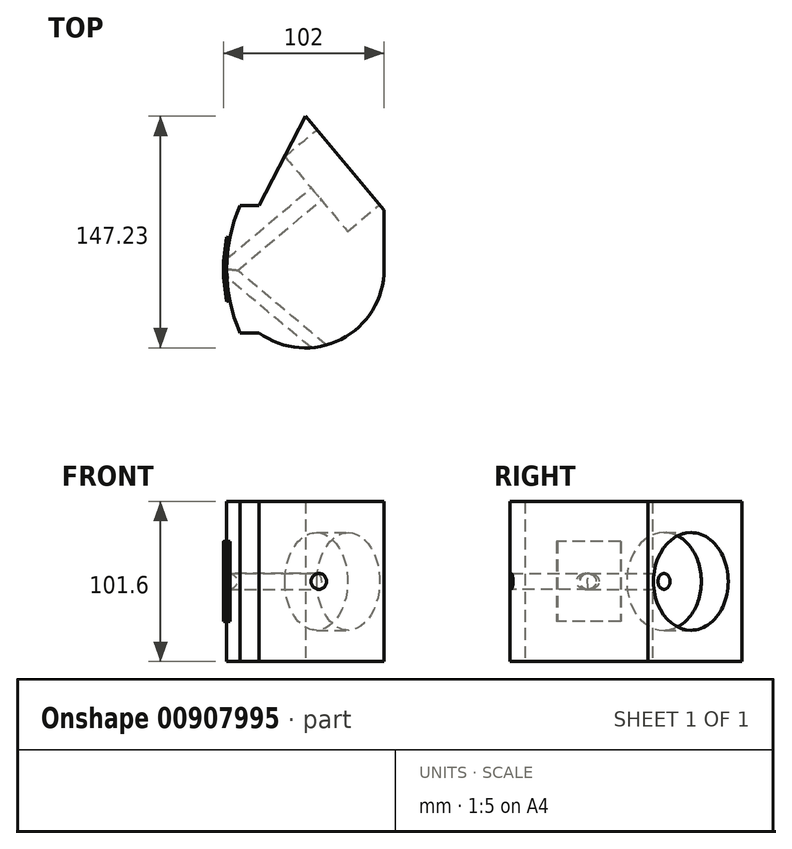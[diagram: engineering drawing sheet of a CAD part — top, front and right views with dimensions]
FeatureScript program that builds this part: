
annotation { "Feature Type Name" : "Feature", "Feature Type Description" : "" }
export const myFeature = defineFeature(function(context is Context, id is Id, definition is map)
    precondition{}
    {
        {
            var Q0;
            Q0=qCreatedBy(makeId("Top.planeOp"),FACE);
            var sketch = newSketch(context, id + "F0", { "sketchPlane" : qUnion([Q0])});
            skCircle(sketch, "E0", {"center": v(0, 0) * mm, "radius": 50 * mm});
            skLineSegment(sketch, "E1", {"start": v(-50, 0) * mm, "end": v(8.68, 49.24) * mm});
            skLineSegment(sketch, "E2", {"start": v(8.68, 49.24) * mm, "end": v(8.68, -49.24) * mm, "construction": true});
            skLineSegment(sketch, "E3", {"start": v(47.6, -81.9) * mm, "end": v(-50, 0) * mm});
            skPoint(sketch, "E4", {"position": v(8.68, 0) * mm});
            skLineSegment(sketch, "E5", {"start": v(-50, 0) * mm, "end": v(-50, 56.97) * mm, "construction": true});
            skLineSegment(sketch, "E6.MirrorCS", {"start": v(-50, 0) * mm, "end": v(-108.68, 49.24) * mm});
            skLineSegment(sketch, "E7", {"start": v(-50, 0) * mm, "end": v(8.68, 0) * mm, "construction": true});
            skLineSegment(sketch, "E8", {"start": v(0, 0) * mm, "end": v(8.68, 49.24) * mm, "construction": true});
            skSolve(sketch);
        }
        {
            var Q0;
            Q0=qCreatedBy(makeId("Top.planeOp"),FACE);
            var sketch = newSketch(context, id + "F1", { "sketchPlane" : qUnion([Q0])});
            skArc(sketch, "E9", {"start": v(-47.98, 20) * mm, "mid": v(-50, 0) * mm, "end": v(-47.98, -20) * mm});
            skArc(sketch, "E10", {"start": v(-49.94, 20.4) * mm, "mid": v(-52, 0) * mm, "end": v(-49.94, -20.4) * mm});
            skLineSegment(sketch, "E11", {"start": v(-49.94, 20.4) * mm, "end": v(-47.98, 20) * mm});
            skLineSegment(sketch, "E12", {"start": v(-47.98, -20) * mm, "end": v(-49.94, -20.4) * mm});
            skSolve(sketch);
        }
        {
            var Q0;
            Q0=qSketchRegion(id+"F1",true);
            extrude(context, id + "F2", {"entities" : qUnion([Q0]), "depth" : 25.4 * mm, "offsetDistance" : 25.4 * mm, "hasSecondDirection" : true, "secondDirectionOppositeDirection" : true, "secondDirectionDepth" : 25.4 * mm});
        }
        {
            var Q0;
            Q0=qCreatedBy(makeId("Top.planeOp"),FACE);
            var sketch = newSketch(context, id + "F3", { "sketchPlane" : qUnion([Q0])});
            skArc(sketch, "E13", {"start": v(-41.48, 40.4) * mm, "mid": v(-50, 0) * mm, "end": v(-41.48, -40.4) * mm});
            skLineSegment(sketch, "E14", {"start": v(-41.48, 40.4) * mm, "end": v(-29.46, 40.4) * mm});
            skLineSegment(sketch, "E15", {"start": v(-41.48, -40.4) * mm, "end": v(-29.46, -40.4) * mm});
            skArc(sketch, "E16", {"start": v(-29.46, -40.4) * mm, "mid": v(22.66, -44.57) * mm, "end": v(50, 0) * mm});
            skLineSegment(sketch, "E17", {"start": v(0, 97.23) * mm, "end": v(50, 37.64) * mm});
            skLineSegment(sketch, "E18", {"start": v(50, 37.64) * mm, "end": v(50, 0) * mm});
            skLineSegment(sketch, "E19", {"start": v(-29.46, 40.4) * mm, "end": v(0, 97.23) * mm});
            skSolve(sketch);
        }
        {
            var Q0;
            Q0=qSketchRegion(id+"F3",true);
            extrude(context, id + "F4", {"entities" : qUnion([Q0]), "depth" : 50.8 * mm, "offsetDistance" : 25.4 * mm, "hasSecondDirection" : true, "secondDirectionOppositeDirection" : true, "secondDirectionDepth" : 50.8 * mm});
        }
        {
            var Q0;
            Q0=makeQuery(id+"F4.opExtrude","SWEPT_FACE",FACE,{"disambiguationData":[OSD([sQuery(id+"F3.wireOp",EDGE,"E17")])]});
            var sketch = newSketch(context, id + "F5", { "sketchPlane" : qUnion([Q0])});
            skCircle(sketch, "E20", {"center": v(32.14, 0) * mm, "radius": 5 * mm});
            skSolve(sketch);
        }
        {
            var Q0;
            Q0=makeQuery(id+"F5.imprint","IMPRINT",FACE,{"disambiguationData":[TD([[makeQuery(id+"F5.imprint","IMPRINT",EDGE,{"derivedFrom":sQuery(id+"F5.wireOp",EDGE,"E20")}),1.0]])]});
            var Q1;
            Q1=sQuery(id+"F5.wireOp",EDGE,"E20");
            extrude(context, id + "F6", {"entities" : qUnion([Q0]), "operationType" : NewBodyOperationType.REMOVE, "surfaceOperationType" : NewSurfaceOperationType.ADD, "surfaceEntities" : qUnion([Q1]), "oppositeDirection" : true, "depth" : 127 * mm, "offsetDistance" : 25.4 * mm});
        }
        {
            var Q0;
            Q0=makeQuery(id+"F4.opExtrude","SWEPT_FACE",FACE,{"disambiguationData":[OSD([sQuery(id+"F3.wireOp",EDGE,"E17")])]});
            var sketch = newSketch(context, id + "F7", { "sketchPlane" : qUnion([Q0])});
            skCircle(sketch, "E21", {"center": v(32.14, 0) * mm, "radius": 31 * mm});
            skSolve(sketch);
        }
        {
            var Q0;
            Q0 = qSketchRegion(id + "F7", true);
            extrude(context, id + "F8", {"entities" : qUnion([Q0]), "operationType" : NewBodyOperationType.REMOVE, "oppositeDirection" : true, "depth" : 26.5 * mm, "offsetDistance" : 25.4 * mm});
        }
        {
            var Q0;
            Q0=qCreatedBy(makeId("Right.planeOp"),FACE);
            var sketch = newSketch(context, id + "F9", { "sketchPlane" : qUnion([Q0])});
            skCircle(sketch, "E22", {"center": v(-41.95, 0) * mm, "radius": 5 * mm});
            skSolve(sketch);
        }
        {
            var Q0;
            Q0 = qSketchRegion(id + "F9", true);
            var Q1;
            Q1=sQuery(id+"F0.wireOp",EDGE,"E3");
            sweep(context, id + "F10", {"operationType" : NewBodyOperationType.REMOVE, "profiles" : qUnion([Q0]), "path" : qUnion([Q1]), "keepProfileOrientation" : true});
        }
    });
